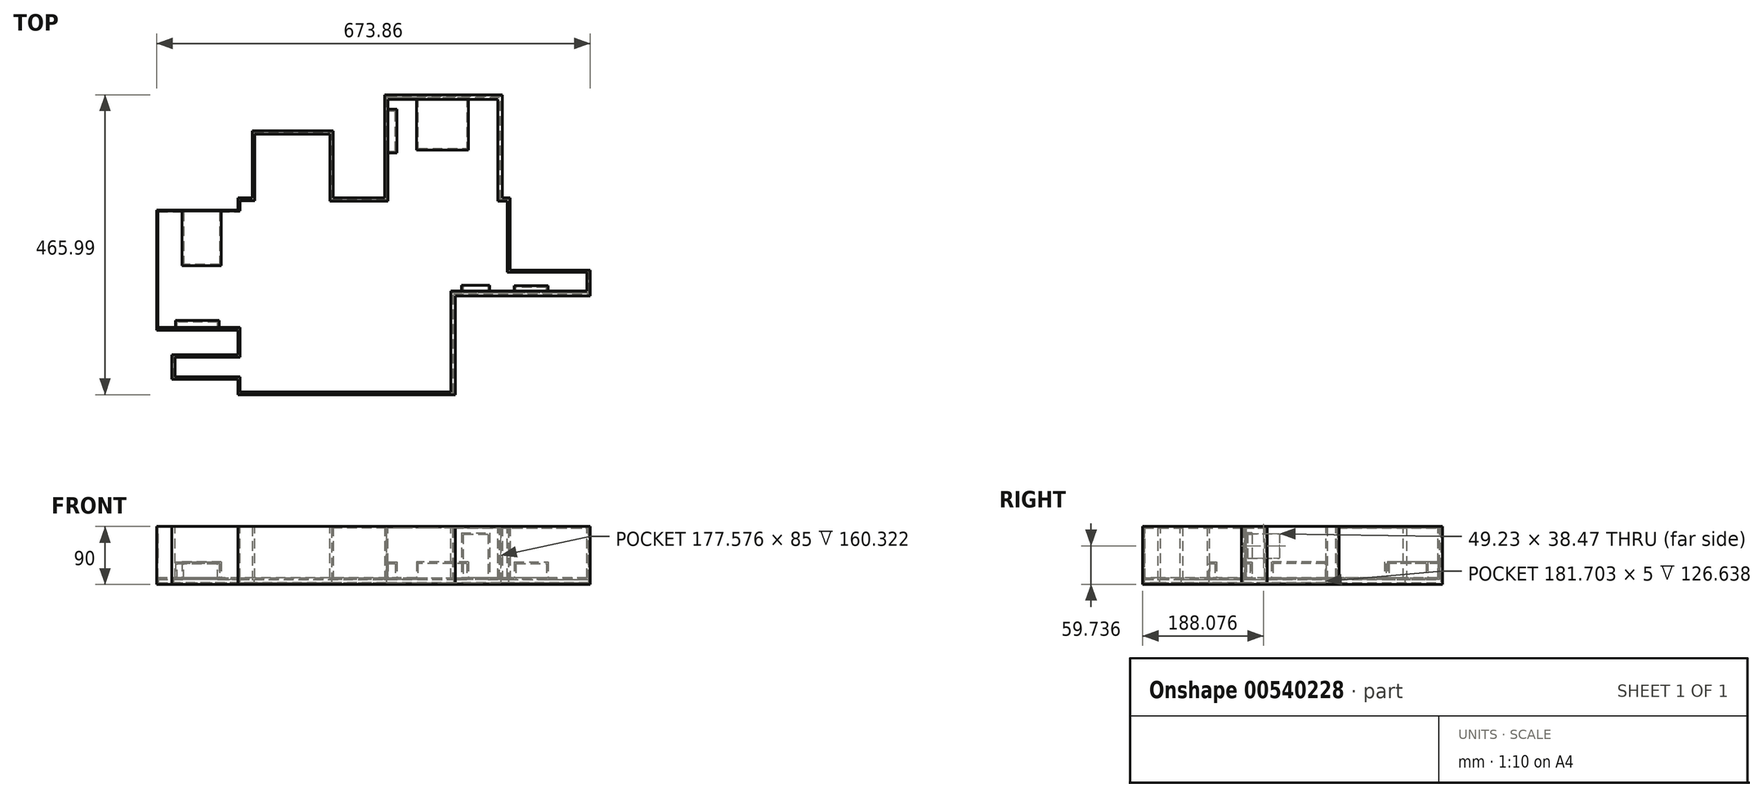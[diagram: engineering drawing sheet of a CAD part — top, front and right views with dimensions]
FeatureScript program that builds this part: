
annotation { "Feature Type Name" : "Feature", "Feature Type Description" : "" }
export const myFeature = defineFeature(function(context is Context, id is Id, definition is map)
    precondition{}
    {
        {
            var Q0;
            Q0=qCreatedBy(makeId("Top.planeOp"),FACE);
            var sketch = newSketch(context, id + "F0", { "sketchPlane" : qUnion([Q0])});
            skLineSegment(sketch, "E0", {"start": v(50.82, -63.76) * mm, "end": v(61.25, -63.76) * mm});
            skLineSegment(sketch, "E1", {"start": v(61.25, -63.76) * mm, "end": v(61.25, -103.76) * mm});
            skLineSegment(sketch, "E2", {"start": v(61.25, -103.76) * mm, "end": v(209.38, -103.76) * mm});
            skLineSegment(sketch, "E3", {"start": v(209.38, -103.76) * mm, "end": v(209.38, -63.76) * mm});
            skLineSegment(sketch, "E4", {"start": v(209.38, -63.76) * mm, "end": v(84.95, -63.76) * mm});
            skLineSegment(sketch, "E5", {"start": v(84.95, -63.76) * mm, "end": v(84.95, 48.36) * mm});
            skLineSegment(sketch, "E6", {"start": v(84.95, 48.36) * mm, "end": v(72.68, 48.36) * mm});
            skLineSegment(sketch, "E7", {"start": v(72.68, 48.36) * mm, "end": v(72.68, 208.68) * mm});
            skLineSegment(sketch, "E8", {"start": v(72.68, 208.68) * mm, "end": v(-109.9, 208.68) * mm});
            skLineSegment(sketch, "E9", {"start": v(-109.9, 208.68) * mm, "end": v(-109.9, 48.36) * mm});
            skLineSegment(sketch, "E10", {"start": v(-109.9, 48.36) * mm, "end": v(23.18, 48.36) * mm});
            skLineSegment(sketch, "E11", {"start": v(-109.9, 48.36) * mm, "end": v(-190.28, 48.36) * mm});
            skLineSegment(sketch, "E12", {"start": v(-190.28, 48.36) * mm, "end": v(-190.28, 152.82) * mm});
            skLineSegment(sketch, "E13", {"start": v(-190.28, 152.82) * mm, "end": v(-315.63, 152.82) * mm});
            skLineSegment(sketch, "E14", {"start": v(-315.63, 152.82) * mm, "end": v(-315.63, 48.36) * mm});
            skLineSegment(sketch, "E15", {"start": v(-315.63, 48.36) * mm, "end": v(-272.48, 48.36) * mm});
            skLineSegment(sketch, "E16", {"start": v(-190.28, 48.36) * mm, "end": v(-238.88, 48.36) * mm});
            skLineSegment(sketch, "E17", {"start": v(-315.63, 48.36) * mm, "end": v(-337.84, 48.36) * mm});
            skLineSegment(sketch, "E18", {"start": v(-337.84, 48.36) * mm, "end": v(-337.84, 29.83) * mm});
            skLineSegment(sketch, "E19", {"start": v(-337.84, 29.83) * mm, "end": v(-464.48, 29.83) * mm});
            skLineSegment(sketch, "E20", {"start": v(-464.48, 29.83) * mm, "end": v(-464.48, -156.87) * mm});
            skLineSegment(sketch, "E21", {"start": v(-464.48, -156.87) * mm, "end": v(-337.84, -156.87) * mm});
            skLineSegment(sketch, "E22", {"start": v(-337.84, -156.87) * mm, "end": v(-337.84, -8.6) * mm});
            skLineSegment(sketch, "E23", {"start": v(-337.84, -156.87) * mm, "end": v(-337.84, -195.13) * mm});
            skLineSegment(sketch, "E24", {"start": v(-337.84, -195.13) * mm, "end": v(-440.57, -195.13) * mm});
            skLineSegment(sketch, "E25", {"start": v(-440.57, -195.13) * mm, "end": v(-440.57, -233.4) * mm});
            skLineSegment(sketch, "E26", {"start": v(-440.57, -233.4) * mm, "end": v(-337.84, -233.4) * mm});
            skLineSegment(sketch, "E27", {"start": v(-337.84, -233.4) * mm, "end": v(-337.84, -257.31) * mm});
            skLineSegment(sketch, "E28", {"start": v(-337.84, -257.31) * mm, "end": v(0, -257.31) * mm});
            skLineSegment(sketch, "E29", {"start": v(0, -257.31) * mm, "end": v(0, -103.76) * mm});
            skLineSegment(sketch, "E30", {"start": v(0, -103.76) * mm, "end": v(61.25, -103.76) * mm});
            skSolve(sketch);
        }
        {
            var Q0;
            Q0=makeQuery(id+"F0.imprint","IMPRINT",FACE,{"disambiguationData":[TD([[makeQuery(id+"F0.imprint","IMPRINT",EDGE,{"derivedFrom":sQuery(id+"F0.wireOp",EDGE,"E2")}),1.0]])]});
            extrude(context, id + "F1", {"entities" : qUnion([Q0]), "depth" : 90 * mm, "offsetDistance" : 25 * mm});
        }
        {
            var Q0;
            Q0=makeQuery(id+"F1.opExtrude","CAP_FACE",FACE,{"disambiguationData":[OSD([sQuery(id+"F0.wireOp",EDGE,"E2"),sQuery(id+"F0.wireOp",EDGE,"E3"),sQuery(id+"F0.wireOp",EDGE,"E4"),sQuery(id+"F0.wireOp",EDGE,"E5"),sQuery(id+"F0.wireOp",EDGE,"E6"),sQuery(id+"F0.wireOp",EDGE,"E7"),sQuery(id+"F0.wireOp",EDGE,"E8"),sQuery(id+"F0.wireOp",EDGE,"E9"),sQuery(id+"F0.wireOp",EDGE,"E11"),sQuery(id+"F0.wireOp",EDGE,"E12"),sQuery(id+"F0.wireOp",EDGE,"E13"),sQuery(id+"F0.wireOp",EDGE,"E14"),sQuery(id+"F0.wireOp",EDGE,"E17"),sQuery(id+"F0.wireOp",EDGE,"E18"),sQuery(id+"F0.wireOp",EDGE,"E19"),sQuery(id+"F0.wireOp",EDGE,"E20"),sQuery(id+"F0.wireOp",EDGE,"E21"),sQuery(id+"F0.wireOp",EDGE,"E23"),sQuery(id+"F0.wireOp",EDGE,"E24"),sQuery(id+"F0.wireOp",EDGE,"E25"),sQuery(id+"F0.wireOp",EDGE,"E26"),sQuery(id+"F0.wireOp",EDGE,"E27"),sQuery(id+"F0.wireOp",EDGE,"E28"),sQuery(id+"F0.wireOp",EDGE,"E29"),sQuery(id+"F0.wireOp",EDGE,"E30")])],"isStart":false});
            var sketch = newSketch(context, id + "F2", { "sketchPlane" : qUnion([Q0])});
            skLineSegment(sketch, "E31", {"start": v(-462.58, 27.99) * mm, "end": v(-462.58, -152.9) * mm});
            skLineSegment(sketch, "E32", {"start": v(-462.58, -152.9) * mm, "end": v(-334.5, -152.9) * mm});
            skLineSegment(sketch, "E33", {"start": v(-334.5, -152.9) * mm, "end": v(-334.5, -198.79) * mm});
            skLineSegment(sketch, "E34", {"start": v(-334.5, -198.79) * mm, "end": v(-435.58, -198.79) * mm});
            skLineSegment(sketch, "E35", {"start": v(-435.58, -198.79) * mm, "end": v(-435.58, -229.23) * mm});
            skLineSegment(sketch, "E36", {"start": v(-435.58, -229.23) * mm, "end": v(-334.5, -229.23) * mm});
            skLineSegment(sketch, "E37", {"start": v(-334.5, -229.23) * mm, "end": v(-334.5, -253.28) * mm});
            skLineSegment(sketch, "E38", {"start": v(-334.5, -253.28) * mm, "end": v(-6.95, -253.28) * mm});
            skLineSegment(sketch, "E39", {"start": v(-6.95, -253.28) * mm, "end": v(-6.95, -96.17) * mm});
            skLineSegment(sketch, "E40", {"start": v(-6.95, -96.17) * mm, "end": v(204.17, -96.17) * mm});
            skLineSegment(sketch, "E41", {"start": v(204.17, -96.17) * mm, "end": v(204.17, -67.2) * mm});
            skLineSegment(sketch, "E42", {"start": v(204.17, -67.2) * mm, "end": v(80.44, -67.2) * mm});
            skLineSegment(sketch, "E43", {"start": v(80.44, -67.2) * mm, "end": v(80.44, 43.27) * mm});
            skLineSegment(sketch, "E44", {"start": v(80.44, 43.27) * mm, "end": v(65.71, 43.27) * mm});
            skLineSegment(sketch, "E45", {"start": v(65.71, 43.27) * mm, "end": v(65.71, 201.86) * mm});
            skLineSegment(sketch, "E46", {"start": v(65.71, 201.86) * mm, "end": v(-104.66, 201.86) * mm});
            skLineSegment(sketch, "E47", {"start": v(-104.66, 201.86) * mm, "end": v(-104.66, 43.27) * mm});
            skLineSegment(sketch, "E48", {"start": v(-104.66, 43.27) * mm, "end": v(-195, 43.27) * mm});
            skLineSegment(sketch, "E49", {"start": v(-195, 43.27) * mm, "end": v(-195, 147.85) * mm});
            skLineSegment(sketch, "E50", {"start": v(-195, 147.85) * mm, "end": v(-311.85, 147.85) * mm});
            skLineSegment(sketch, "E51", {"start": v(-311.85, 147.85) * mm, "end": v(-311.85, 44.25) * mm});
            skLineSegment(sketch, "E52", {"start": v(-311.85, 44.25) * mm, "end": v(-334.5, 44.25) * mm});
            skLineSegment(sketch, "E53", {"start": v(-334.5, 44.25) * mm, "end": v(-334.5, 27.99) * mm});
            skLineSegment(sketch, "E54", {"start": v(-334.5, 27.99) * mm, "end": v(-462.58, 27.99) * mm});
            skSolve(sketch);
        }
        {
            var Q0;
            Q0 = qSketchRegion(id + "F2", true);
            extrude(context, id + "F3", {"entities" : qUnion([Q0]), "operationType" : NewBodyOperationType.REMOVE, "oppositeDirection" : true, "depth" : 80 * mm, "offsetDistance" : 25 * mm});
        }
        {
            var Q0;
            Q0=makeQuery(id+"F3.boolean.opBoolean","COPY",FACE,{"derivedFrom":makeQuery(id+"F3.opExtrude","CAP_FACE",FACE,{"disambiguationData":[OSD([sQuery(id+"F2.wireOp",EDGE,"E31"),sQuery(id+"F2.wireOp",EDGE,"E32"),sQuery(id+"F2.wireOp",EDGE,"E33"),sQuery(id+"F2.wireOp",EDGE,"E34"),sQuery(id+"F2.wireOp",EDGE,"E35"),sQuery(id+"F2.wireOp",EDGE,"E36"),sQuery(id+"F2.wireOp",EDGE,"E37"),sQuery(id+"F2.wireOp",EDGE,"E38"),sQuery(id+"F2.wireOp",EDGE,"E39"),sQuery(id+"F2.wireOp",EDGE,"E40"),sQuery(id+"F2.wireOp",EDGE,"E41"),sQuery(id+"F2.wireOp",EDGE,"E42"),sQuery(id+"F2.wireOp",EDGE,"E43"),sQuery(id+"F2.wireOp",EDGE,"E44"),sQuery(id+"F2.wireOp",EDGE,"E45"),sQuery(id+"F2.wireOp",EDGE,"E46"),sQuery(id+"F2.wireOp",EDGE,"E47"),sQuery(id+"F2.wireOp",EDGE,"E48"),sQuery(id+"F2.wireOp",EDGE,"E49"),sQuery(id+"F2.wireOp",EDGE,"E50"),sQuery(id+"F2.wireOp",EDGE,"E51"),sQuery(id+"F2.wireOp",EDGE,"E52"),sQuery(id+"F2.wireOp",EDGE,"E53"),sQuery(id+"F2.wireOp",EDGE,"E54")])],"isStart":false})});
            var sketch = newSketch(context, id + "F4", { "sketchPlane" : qUnion([Q0])});
            skLineSegment(sketch, "E55", {"start": v(-311.85, 44.25) * mm, "end": v(-269.44, 44.25) * mm});
            skLineSegment(sketch, "E56", {"start": v(-195, 43.27) * mm, "end": v(-235.64, 43.27) * mm});
            skLineSegment(sketch, "E57", {"start": v(-334.5, 27.99) * mm, "end": v(-334.5, -3.08) * mm});
            skLineSegment(sketch, "E58", {"start": v(-334.5, -152.9) * mm, "end": v(-334.5, -35.5) * mm});
            skLineSegment(sketch, "E59", {"start": v(-6.95, -96.17) * mm, "end": v(-6.95, -67.2) * mm});
            skLineSegment(sketch, "E60", {"start": v(80.44, -67.2) * mm, "end": v(14.58, -67.2) * mm});
            skLineSegment(sketch, "E61", {"start": v(-104.66, 43.27) * mm, "end": v(5.22, 43.27) * mm});
            skLineSegment(sketch, "E62", {"start": v(65.71, 43.27) * mm, "end": v(44.78, 43.27) * mm});
            skSolve(sketch);
        }
        {
            var Q0;
            Q0=sQuery(id+"F4.wireOp",EDGE,"E61");
            extrude(context, id + "F5", {"bodyType" : ToolBodyType.SURFACE, "surfaceEntities" : qUnion([Q0]), "depth" : 80 * mm, "offsetDistance" : 25 * mm});
        }
        {
            var Q0;
            Q0=makeQuery(id+"F3.boolean.opBoolean","COPY",FACE,{"derivedFrom":makeQuery(id+"F3.opExtrude","CAP_FACE",FACE,{"disambiguationData":[OSD([sQuery(id+"F2.wireOp",EDGE,"E31"),sQuery(id+"F2.wireOp",EDGE,"E32"),sQuery(id+"F2.wireOp",EDGE,"E33"),sQuery(id+"F2.wireOp",EDGE,"E34"),sQuery(id+"F2.wireOp",EDGE,"E35"),sQuery(id+"F2.wireOp",EDGE,"E36"),sQuery(id+"F2.wireOp",EDGE,"E37"),sQuery(id+"F2.wireOp",EDGE,"E38"),sQuery(id+"F2.wireOp",EDGE,"E39"),sQuery(id+"F2.wireOp",EDGE,"E40"),sQuery(id+"F2.wireOp",EDGE,"E41"),sQuery(id+"F2.wireOp",EDGE,"E42"),sQuery(id+"F2.wireOp",EDGE,"E43"),sQuery(id+"F2.wireOp",EDGE,"E44"),sQuery(id+"F2.wireOp",EDGE,"E45"),sQuery(id+"F2.wireOp",EDGE,"E46"),sQuery(id+"F2.wireOp",EDGE,"E47"),sQuery(id+"F2.wireOp",EDGE,"E48"),sQuery(id+"F2.wireOp",EDGE,"E49"),sQuery(id+"F2.wireOp",EDGE,"E50"),sQuery(id+"F2.wireOp",EDGE,"E51"),sQuery(id+"F2.wireOp",EDGE,"E52"),sQuery(id+"F2.wireOp",EDGE,"E53"),sQuery(id+"F2.wireOp",EDGE,"E54")])],"isStart":false})});
            var sketch = newSketch(context, id + "F6", { "sketchPlane" : qUnion([Q0])});
            skLineSegment(sketch, "E63", {"start": v(-311.85, 44.25) * mm, "end": v(-244.66, 44.25) * mm});
            skSolve(sketch);
        }
        {
            var Q0;
            Q0=sQuery(id+"F6.wireOp",EDGE,"E63");
            extrude(context, id + "F7", {"bodyType" : ToolBodyType.SURFACE, "surfaceEntities" : qUnion([Q0]), "depth" : 80 * mm, "offsetDistance" : 25 * mm});
        }
        {
            var Q0;
            Q0=makeQuery(id+"F3.boolean.opBoolean","COPY",FACE,{"derivedFrom":makeQuery(id+"F3.opExtrude","CAP_FACE",FACE,{"disambiguationData":[OSD([sQuery(id+"F2.wireOp",EDGE,"E31"),sQuery(id+"F2.wireOp",EDGE,"E32"),sQuery(id+"F2.wireOp",EDGE,"E33"),sQuery(id+"F2.wireOp",EDGE,"E34"),sQuery(id+"F2.wireOp",EDGE,"E35"),sQuery(id+"F2.wireOp",EDGE,"E36"),sQuery(id+"F2.wireOp",EDGE,"E37"),sQuery(id+"F2.wireOp",EDGE,"E38"),sQuery(id+"F2.wireOp",EDGE,"E39"),sQuery(id+"F2.wireOp",EDGE,"E40"),sQuery(id+"F2.wireOp",EDGE,"E41"),sQuery(id+"F2.wireOp",EDGE,"E42"),sQuery(id+"F2.wireOp",EDGE,"E43"),sQuery(id+"F2.wireOp",EDGE,"E44"),sQuery(id+"F2.wireOp",EDGE,"E45"),sQuery(id+"F2.wireOp",EDGE,"E46"),sQuery(id+"F2.wireOp",EDGE,"E47"),sQuery(id+"F2.wireOp",EDGE,"E48"),sQuery(id+"F2.wireOp",EDGE,"E49"),sQuery(id+"F2.wireOp",EDGE,"E50"),sQuery(id+"F2.wireOp",EDGE,"E51"),sQuery(id+"F2.wireOp",EDGE,"E52"),sQuery(id+"F2.wireOp",EDGE,"E53"),sQuery(id+"F2.wireOp",EDGE,"E54")])],"isStart":false})});
            var sketch = newSketch(context, id + "F8", { "sketchPlane" : qUnion([Q0])});
            skLineSegment(sketch, "E64", {"start": v(-6.95, -96.17) * mm, "end": v(-6.95, -67.2) * mm});
            skSolve(sketch);
        }
        {
            var Q0;
            Q0=sQuery(id+"F8.wireOp",EDGE,"E64");
            extrude(context, id + "F9", {"bodyType" : ToolBodyType.SURFACE, "surfaceEntities" : qUnion([Q0]), "depth" : 80 * mm, "offsetDistance" : 25 * mm});
        }
        {
            var Q0;
            Q0=makeQuery(id+"F3.boolean.opBoolean","COPY",FACE,{"derivedFrom":makeQuery(id+"F3.opExtrude","CAP_FACE",FACE,{"disambiguationData":[OSD([sQuery(id+"F2.wireOp",EDGE,"E31"),sQuery(id+"F2.wireOp",EDGE,"E32"),sQuery(id+"F2.wireOp",EDGE,"E33"),sQuery(id+"F2.wireOp",EDGE,"E34"),sQuery(id+"F2.wireOp",EDGE,"E35"),sQuery(id+"F2.wireOp",EDGE,"E36"),sQuery(id+"F2.wireOp",EDGE,"E37"),sQuery(id+"F2.wireOp",EDGE,"E38"),sQuery(id+"F2.wireOp",EDGE,"E39"),sQuery(id+"F2.wireOp",EDGE,"E40"),sQuery(id+"F2.wireOp",EDGE,"E41"),sQuery(id+"F2.wireOp",EDGE,"E42"),sQuery(id+"F2.wireOp",EDGE,"E43"),sQuery(id+"F2.wireOp",EDGE,"E44"),sQuery(id+"F2.wireOp",EDGE,"E45"),sQuery(id+"F2.wireOp",EDGE,"E46"),sQuery(id+"F2.wireOp",EDGE,"E47"),sQuery(id+"F2.wireOp",EDGE,"E48"),sQuery(id+"F2.wireOp",EDGE,"E49"),sQuery(id+"F2.wireOp",EDGE,"E50"),sQuery(id+"F2.wireOp",EDGE,"E51"),sQuery(id+"F2.wireOp",EDGE,"E52"),sQuery(id+"F2.wireOp",EDGE,"E53"),sQuery(id+"F2.wireOp",EDGE,"E54")])],"isStart":false})});
            var sketch = newSketch(context, id + "F10", { "sketchPlane" : qUnion([Q0])});
            skLineSegment(sketch, "E65", {"start": v(80.44, -67.2) * mm, "end": v(29.85, -67.2) * mm});
            skSolve(sketch);
        }
        {
            var Q0;
            Q0=sQuery(id+"F10.wireOp",EDGE,"E65");
            extrude(context, id + "F11", {"bodyType" : ToolBodyType.SURFACE, "surfaceEntities" : qUnion([Q0]), "depth" : 80 * mm, "offsetDistance" : 25 * mm});
        }
        {
            var Q0;
            Q0=makeQuery(id+"F3.boolean.opBoolean","COPY",FACE,{"derivedFrom":makeQuery(id+"F3.opExtrude","CAP_FACE",FACE,{"disambiguationData":[OSD([sQuery(id+"F2.wireOp",EDGE,"E31"),sQuery(id+"F2.wireOp",EDGE,"E32"),sQuery(id+"F2.wireOp",EDGE,"E33"),sQuery(id+"F2.wireOp",EDGE,"E34"),sQuery(id+"F2.wireOp",EDGE,"E35"),sQuery(id+"F2.wireOp",EDGE,"E36"),sQuery(id+"F2.wireOp",EDGE,"E37"),sQuery(id+"F2.wireOp",EDGE,"E38"),sQuery(id+"F2.wireOp",EDGE,"E39"),sQuery(id+"F2.wireOp",EDGE,"E40"),sQuery(id+"F2.wireOp",EDGE,"E41"),sQuery(id+"F2.wireOp",EDGE,"E42"),sQuery(id+"F2.wireOp",EDGE,"E43"),sQuery(id+"F2.wireOp",EDGE,"E44"),sQuery(id+"F2.wireOp",EDGE,"E45"),sQuery(id+"F2.wireOp",EDGE,"E46"),sQuery(id+"F2.wireOp",EDGE,"E47"),sQuery(id+"F2.wireOp",EDGE,"E48"),sQuery(id+"F2.wireOp",EDGE,"E49"),sQuery(id+"F2.wireOp",EDGE,"E50"),sQuery(id+"F2.wireOp",EDGE,"E51"),sQuery(id+"F2.wireOp",EDGE,"E52"),sQuery(id+"F2.wireOp",EDGE,"E53"),sQuery(id+"F2.wireOp",EDGE,"E54")])],"isStart":false})});
            var sketch = newSketch(context, id + "F12", { "sketchPlane" : qUnion([Q0])});
            skLineSegment(sketch, "E66", {"start": v(-334.5, -152.9) * mm, "end": v(-334.5, -19.02) * mm});
            skSolve(sketch);
        }
        {
            var Q0;
            Q0=sQuery(id+"F12.wireOp",EDGE,"E66");
            extrude(context, id + "F13", {"bodyType" : ToolBodyType.SURFACE, "surfaceEntities" : qUnion([Q0]), "depth" : 80 * mm, "offsetDistance" : 25 * mm});
        }
        {
            var Q0;
            Q0=makeQuery(id+"F3.boolean.opBoolean","COPY",FACE,{"derivedFrom":makeQuery(id+"F3.opExtrude","CAP_FACE",FACE,{"disambiguationData":[OSD([sQuery(id+"F2.wireOp",EDGE,"E31"),sQuery(id+"F2.wireOp",EDGE,"E32"),sQuery(id+"F2.wireOp",EDGE,"E33"),sQuery(id+"F2.wireOp",EDGE,"E34"),sQuery(id+"F2.wireOp",EDGE,"E35"),sQuery(id+"F2.wireOp",EDGE,"E36"),sQuery(id+"F2.wireOp",EDGE,"E37"),sQuery(id+"F2.wireOp",EDGE,"E38"),sQuery(id+"F2.wireOp",EDGE,"E39"),sQuery(id+"F2.wireOp",EDGE,"E40"),sQuery(id+"F2.wireOp",EDGE,"E41"),sQuery(id+"F2.wireOp",EDGE,"E42"),sQuery(id+"F2.wireOp",EDGE,"E43"),sQuery(id+"F2.wireOp",EDGE,"E44"),sQuery(id+"F2.wireOp",EDGE,"E45"),sQuery(id+"F2.wireOp",EDGE,"E46"),sQuery(id+"F2.wireOp",EDGE,"E47"),sQuery(id+"F2.wireOp",EDGE,"E48"),sQuery(id+"F2.wireOp",EDGE,"E49"),sQuery(id+"F2.wireOp",EDGE,"E50"),sQuery(id+"F2.wireOp",EDGE,"E51"),sQuery(id+"F2.wireOp",EDGE,"E52"),sQuery(id+"F2.wireOp",EDGE,"E53"),sQuery(id+"F2.wireOp",EDGE,"E54")])],"isStart":false})});
            var sketch = newSketch(context, id + "F14", { "sketchPlane" : qUnion([Q0])});
            skLineSegment(sketch, "E67.bottom", {"start": v(-363.9, 27.99) * mm, "end": v(-424.67, 27.99) * mm});
            skLineSegment(sketch, "E67.top", {"start": v(-363.9, -57.1) * mm, "end": v(-424.67, -57.1) * mm});
            skLineSegment(sketch, "E67.left", {"start": v(-363.9, 27.99) * mm, "end": v(-363.9, -57.1) * mm});
            skLineSegment(sketch, "E67.right", {"start": v(-424.67, 27.99) * mm, "end": v(-424.67, -57.1) * mm});
            skLineSegment(sketch, "E68.bottom", {"start": v(-367.42, -152.9) * mm, "end": v(-434.93, -152.9) * mm});
            skLineSegment(sketch, "E68.top", {"start": v(-367.42, -142.06) * mm, "end": v(-434.93, -142.06) * mm});
            skLineSegment(sketch, "E68.left", {"start": v(-367.42, -152.9) * mm, "end": v(-367.42, -142.06) * mm});
            skLineSegment(sketch, "E68.right", {"start": v(-434.93, -152.9) * mm, "end": v(-434.93, -142.06) * mm});
            skSolve(sketch);
        }
        {
            var Q0;
            Q0=makeQuery(id+"F14.imprint","IMPRINT",FACE,{"disambiguationData":[TD([[makeQuery(id+"F14.imprint","IMPRINT",EDGE,{"derivedFrom":sQuery(id+"F14.wireOp",EDGE,"E67.bottom")}),1.0]])]});
            var Q1;
            Q1=makeQuery(id+"F14.imprint","IMPRINT",FACE,{"disambiguationData":[TD([[makeQuery(id+"F14.imprint","IMPRINT",EDGE,{"derivedFrom":sQuery(id+"F14.wireOp",EDGE,"E68.bottom")}),1.0]])]});
            extrude(context, id + "F15", {"entities" : qUnion([Q0, Q1]), "operationType" : NewBodyOperationType.ADD, "depth" : 25 * mm, "offsetDistance" : 25 * mm});
        }
        {
            var Q0;
            Q0=makeQuery(id+"F3.boolean.opBoolean","COPY",FACE,{"derivedFrom":makeQuery(id+"F3.opExtrude","SWEPT_FACE",FACE,{"disambiguationData":[OSD([sQuery(id+"F2.wireOp",EDGE,"E31")])]})});
            var sketch = newSketch(context, id + "F16", { "sketchPlane" : qUnion([Q0])});
            skLineSegment(sketch, "E69.bottom", {"start": v(-93.85, 78.97) * mm, "end": v(-44.62, 78.97) * mm});
            skLineSegment(sketch, "E69.top", {"start": v(-93.85, 40.5) * mm, "end": v(-44.62, 40.5) * mm});
            skLineSegment(sketch, "E69.left", {"start": v(-93.85, 78.97) * mm, "end": v(-93.85, 40.5) * mm});
            skLineSegment(sketch, "E69.right", {"start": v(-44.62, 78.97) * mm, "end": v(-44.62, 40.5) * mm});
            skSolve(sketch);
        }
        {
            var Q0;
            Q0 = qSketchRegion(id + "F16", true);
            extrude(context, id + "F17", {"entities" : qUnion([Q0]), "operationType" : NewBodyOperationType.REMOVE, "oppositeDirection" : true, "depth" : 25 * mm, "offsetDistance" : 25 * mm});
        }
        {
            var Q0;
            Q0=makeQuery(id+"F3.boolean.opBoolean","COPY",FACE,{"derivedFrom":makeQuery(id+"F3.opExtrude","CAP_FACE",FACE,{"disambiguationData":[OSD([sQuery(id+"F2.wireOp",EDGE,"E31"),sQuery(id+"F2.wireOp",EDGE,"E32"),sQuery(id+"F2.wireOp",EDGE,"E33"),sQuery(id+"F2.wireOp",EDGE,"E34"),sQuery(id+"F2.wireOp",EDGE,"E35"),sQuery(id+"F2.wireOp",EDGE,"E36"),sQuery(id+"F2.wireOp",EDGE,"E37"),sQuery(id+"F2.wireOp",EDGE,"E38"),sQuery(id+"F2.wireOp",EDGE,"E39"),sQuery(id+"F2.wireOp",EDGE,"E40"),sQuery(id+"F2.wireOp",EDGE,"E41"),sQuery(id+"F2.wireOp",EDGE,"E42"),sQuery(id+"F2.wireOp",EDGE,"E43"),sQuery(id+"F2.wireOp",EDGE,"E44"),sQuery(id+"F2.wireOp",EDGE,"E45"),sQuery(id+"F2.wireOp",EDGE,"E46"),sQuery(id+"F2.wireOp",EDGE,"E47"),sQuery(id+"F2.wireOp",EDGE,"E48"),sQuery(id+"F2.wireOp",EDGE,"E49"),sQuery(id+"F2.wireOp",EDGE,"E50"),sQuery(id+"F2.wireOp",EDGE,"E51"),sQuery(id+"F2.wireOp",EDGE,"E52"),sQuery(id+"F2.wireOp",EDGE,"E53"),sQuery(id+"F2.wireOp",EDGE,"E54")])],"isStart":false})});
            var sketch = newSketch(context, id + "F18", { "sketchPlane" : qUnion([Q0])});
            skLineSegment(sketch, "E70.bottom", {"start": v(-60.75, 201.86) * mm, "end": v(20.42, 201.86) * mm});
            skLineSegment(sketch, "E70.top", {"start": v(-60.75, 123.17) * mm, "end": v(20.42, 123.17) * mm});
            skLineSegment(sketch, "E70.left", {"start": v(-60.75, 201.86) * mm, "end": v(-60.75, 123.17) * mm});
            skLineSegment(sketch, "E70.right", {"start": v(20.42, 201.86) * mm, "end": v(20.42, 123.17) * mm});
            skLineSegment(sketch, "E71.bottom", {"start": v(-104.66, 118.6) * mm, "end": v(-90.88, 118.6) * mm});
            skLineSegment(sketch, "E71.top", {"start": v(-104.66, 186.14) * mm, "end": v(-90.88, 186.14) * mm});
            skLineSegment(sketch, "E71.left", {"start": v(-104.66, 118.6) * mm, "end": v(-104.66, 186.14) * mm});
            skLineSegment(sketch, "E71.right", {"start": v(-90.88, 118.6) * mm, "end": v(-90.88, 186.14) * mm});
            skSolve(sketch);
        }
        {
            var Q0;
            Q0 = qSketchRegion(id + "F18", true);
            extrude(context, id + "F19", {"entities" : qUnion([Q0]), "operationType" : NewBodyOperationType.ADD, "depth" : 25 * mm, "offsetDistance" : 25 * mm});
        }
        {
            var Q0;
            Q0=makeQuery(id+"F3.boolean.opBoolean","COPY",FACE,{"derivedFrom":makeQuery(id+"F3.opExtrude","CAP_FACE",FACE,{"disambiguationData":[OSD([sQuery(id+"F2.wireOp",EDGE,"E31"),sQuery(id+"F2.wireOp",EDGE,"E32"),sQuery(id+"F2.wireOp",EDGE,"E33"),sQuery(id+"F2.wireOp",EDGE,"E34"),sQuery(id+"F2.wireOp",EDGE,"E35"),sQuery(id+"F2.wireOp",EDGE,"E36"),sQuery(id+"F2.wireOp",EDGE,"E37"),sQuery(id+"F2.wireOp",EDGE,"E38"),sQuery(id+"F2.wireOp",EDGE,"E39"),sQuery(id+"F2.wireOp",EDGE,"E40"),sQuery(id+"F2.wireOp",EDGE,"E41"),sQuery(id+"F2.wireOp",EDGE,"E42"),sQuery(id+"F2.wireOp",EDGE,"E43"),sQuery(id+"F2.wireOp",EDGE,"E44"),sQuery(id+"F2.wireOp",EDGE,"E45"),sQuery(id+"F2.wireOp",EDGE,"E46"),sQuery(id+"F2.wireOp",EDGE,"E47"),sQuery(id+"F2.wireOp",EDGE,"E48"),sQuery(id+"F2.wireOp",EDGE,"E49"),sQuery(id+"F2.wireOp",EDGE,"E50"),sQuery(id+"F2.wireOp",EDGE,"E51"),sQuery(id+"F2.wireOp",EDGE,"E52"),sQuery(id+"F2.wireOp",EDGE,"E53"),sQuery(id+"F2.wireOp",EDGE,"E54")])],"isStart":false})});
            var sketch = newSketch(context, id + "F20", { "sketchPlane" : qUnion([Q0])});
            skLineSegment(sketch, "E72.bottom", {"start": v(143, -96.17) * mm, "end": v(68.76, -96.17) * mm});
            skLineSegment(sketch, "E72.top", {"start": v(143, -87.13) * mm, "end": v(68.76, -87.13) * mm});
            skLineSegment(sketch, "E72.left", {"start": v(143, -96.17) * mm, "end": v(143, -87.13) * mm});
            skLineSegment(sketch, "E72.right", {"start": v(68.76, -96.17) * mm, "end": v(68.76, -87.13) * mm});
            skLineSegment(sketch, "E73.bottom", {"start": v(53.16, -87.13) * mm, "end": v(9.15, -87.13) * mm});
            skLineSegment(sketch, "E73.top", {"start": v(53.16, -96.17) * mm, "end": v(9.15, -96.17) * mm});
            skLineSegment(sketch, "E73.left", {"start": v(53.16, -87.13) * mm, "end": v(53.16, -96.17) * mm});
            skLineSegment(sketch, "E73.right", {"start": v(9.15, -87.13) * mm, "end": v(9.15, -96.17) * mm});
            skSolve(sketch);
        }
        {
            var Q0;
            Q0=makeQuery(id+"F20.imprint","IMPRINT",FACE,{"disambiguationData":[TD([[makeQuery(id+"F20.imprint","IMPRINT",EDGE,{"derivedFrom":sQuery(id+"F20.wireOp",EDGE,"E73.bottom")}),1.0]])]});
            extrude(context, id + "F21", {"entities" : qUnion([Q0]), "operationType" : NewBodyOperationType.ADD, "depth" : 70 * mm, "offsetDistance" : 25 * mm});
        }
        {
            var Q0;
            Q0=makeQuery(id+"F3.boolean.opBoolean","COPY",FACE,{"derivedFrom":makeQuery(id+"F3.opExtrude","CAP_FACE",FACE,{"disambiguationData":[OSD([sQuery(id+"F2.wireOp",EDGE,"E31"),sQuery(id+"F2.wireOp",EDGE,"E32"),sQuery(id+"F2.wireOp",EDGE,"E33"),sQuery(id+"F2.wireOp",EDGE,"E34"),sQuery(id+"F2.wireOp",EDGE,"E35"),sQuery(id+"F2.wireOp",EDGE,"E36"),sQuery(id+"F2.wireOp",EDGE,"E37"),sQuery(id+"F2.wireOp",EDGE,"E38"),sQuery(id+"F2.wireOp",EDGE,"E39"),sQuery(id+"F2.wireOp",EDGE,"E40"),sQuery(id+"F2.wireOp",EDGE,"E41"),sQuery(id+"F2.wireOp",EDGE,"E42"),sQuery(id+"F2.wireOp",EDGE,"E43"),sQuery(id+"F2.wireOp",EDGE,"E44"),sQuery(id+"F2.wireOp",EDGE,"E45"),sQuery(id+"F2.wireOp",EDGE,"E46"),sQuery(id+"F2.wireOp",EDGE,"E47"),sQuery(id+"F2.wireOp",EDGE,"E48"),sQuery(id+"F2.wireOp",EDGE,"E49"),sQuery(id+"F2.wireOp",EDGE,"E50"),sQuery(id+"F2.wireOp",EDGE,"E51"),sQuery(id+"F2.wireOp",EDGE,"E52"),sQuery(id+"F2.wireOp",EDGE,"E53"),sQuery(id+"F2.wireOp",EDGE,"E54")])],"isStart":false})});
            var sketch = newSketch(context, id + "F22", { "sketchPlane" : qUnion([Q0])});
            skLineSegment(sketch, "E74.bottom", {"start": v(143.83, -96.17) * mm, "end": v(91.5, -96.17) * mm});
            skLineSegment(sketch, "E74.top", {"start": v(143.83, -87.69) * mm, "end": v(91.5, -87.69) * mm});
            skLineSegment(sketch, "E74.left", {"start": v(143.83, -96.17) * mm, "end": v(143.83, -87.69) * mm});
            skLineSegment(sketch, "E74.right", {"start": v(91.5, -96.17) * mm, "end": v(91.5, -87.69) * mm});
            skSolve(sketch);
        }
        {
            var Q0;
            Q0=makeQuery(id+"F22.imprint","IMPRINT",FACE,{"disambiguationData":[TD([[makeQuery(id+"F22.imprint","IMPRINT",EDGE,{"derivedFrom":sQuery(id+"F22.wireOp",EDGE,"E74.bottom")}),1.0]])]});
            extrude(context, id + "F23", {"entities" : qUnion([Q0]), "operationType" : NewBodyOperationType.ADD, "depth" : 25 * mm, "offsetDistance" : 25 * mm});
        }
        {
            var Q0;
            Q0=makeQuery(id+"F21.opExtrude","SWEPT_FACE",FACE,{"disambiguationData":[OSD([sQuery(id+"F20.wireOp",EDGE,"E73.bottom")])]});
            shell(context, id + "F24", {"entities" : qUnion([Q0]), "thickness" : 2.5 * mm});
        }
    });
